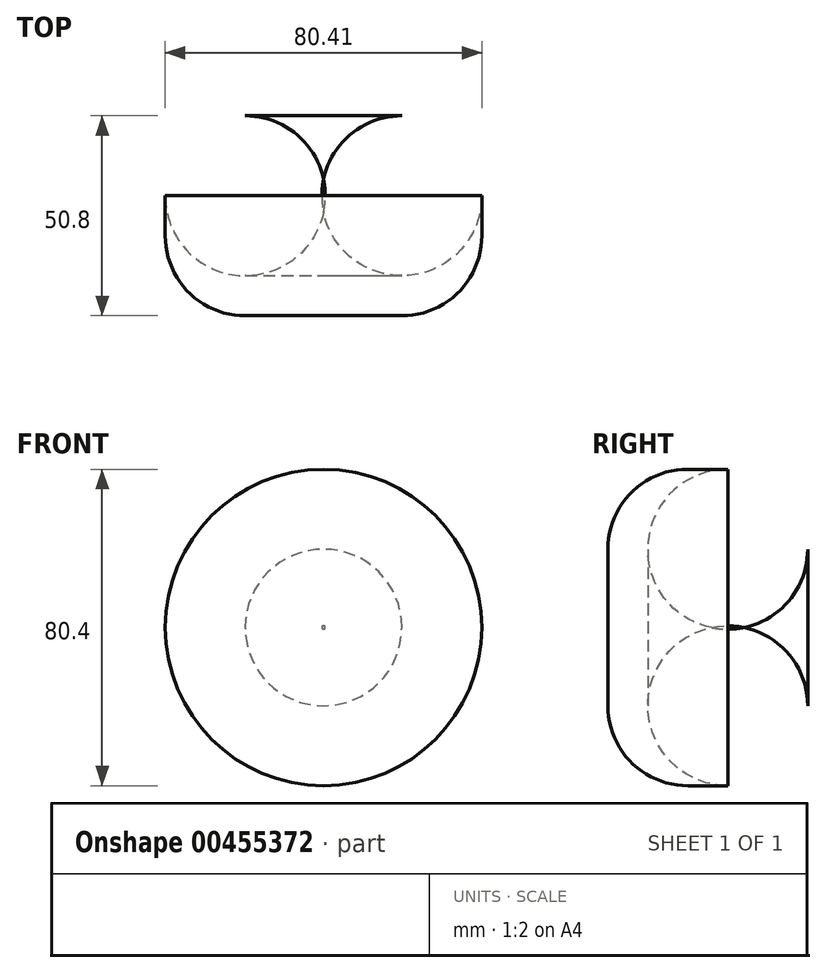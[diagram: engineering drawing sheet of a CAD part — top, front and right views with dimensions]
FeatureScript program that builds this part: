
annotation { "Feature Type Name" : "Feature", "Feature Type Description" : "" }
export const myFeature = defineFeature(function(context is Context, id is Id, definition is map)
    precondition{}
    {
        {
            var Q0;
            Q0=qCreatedBy(makeId("Front.planeOp"),FACE);
            var sketch = newSketch(context, id + "F0", { "sketchPlane" : qUnion([Q0])});
            skCircle(sketch, "E0", {"center": v(-17, 12.41) * mm, "radius": 40.2 * mm});
            skSolve(sketch);
        }
        {
            var Q0;
            Q0 = qSketchRegion(id + "F0", true);
            extrude(context, id + "F1", {"entities" : qUnion([Q0]), "depth" : 50.8 * mm});
        }
        {
            var Q0;
            Q0=makeQuery(id+"F1.opExtrude","SWEPT_FACE",FACE,{"disambiguationData":[OSD([sQuery(id+"F0.wireOp",EDGE,"E0")])]});
            fillet(context, id + "F2", {"entities" : qUnion([Q0]), "radius" : 20.32 * mm, "tangentPropagation" : true, "allowEdgeOverflow" : false});
        }
    });
